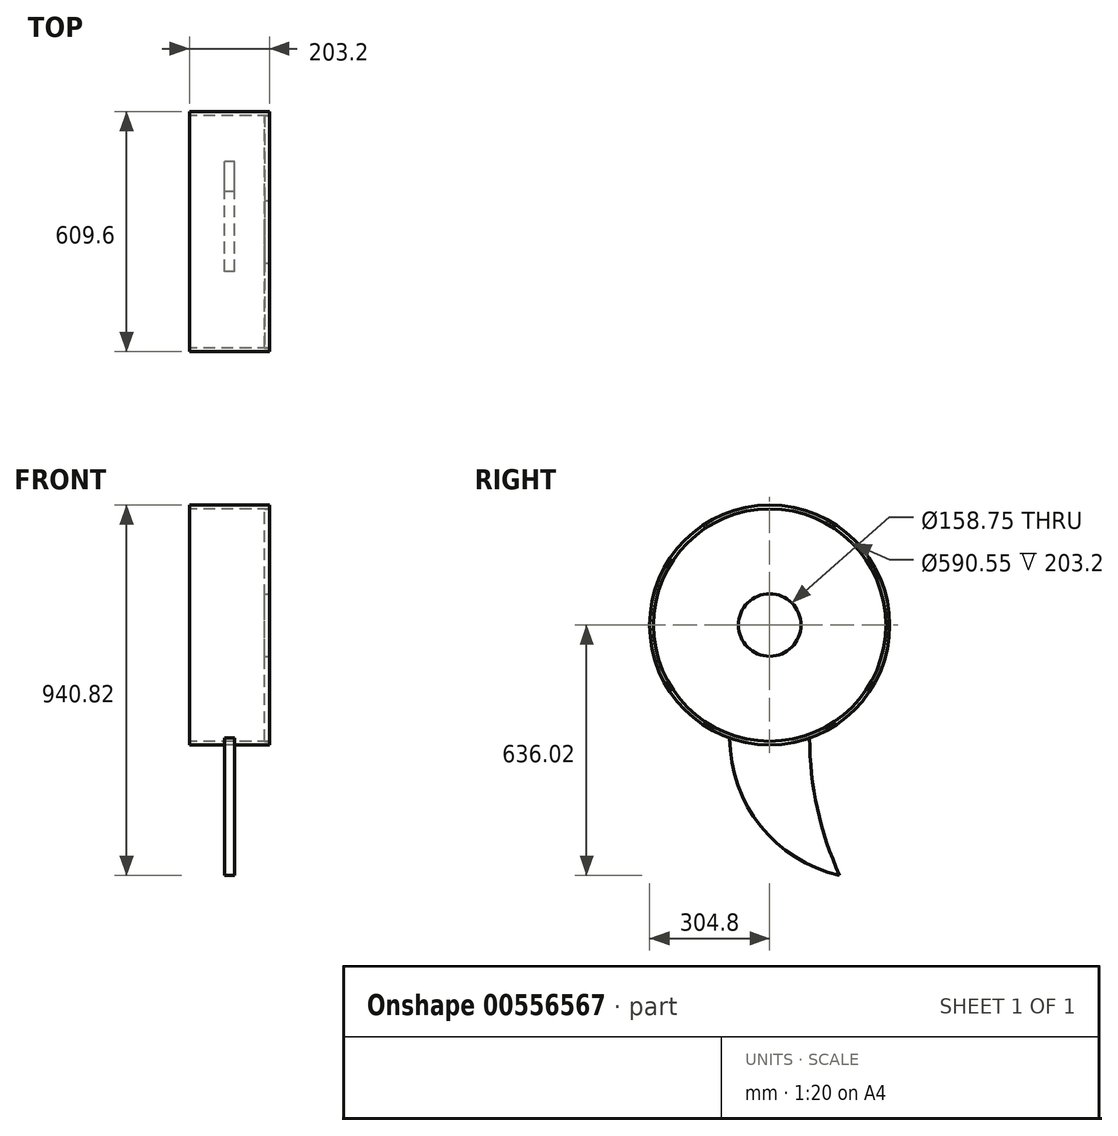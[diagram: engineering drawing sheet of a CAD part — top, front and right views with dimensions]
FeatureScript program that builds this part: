
annotation { "Feature Type Name" : "Feature", "Feature Type Description" : "" }
export const myFeature = defineFeature(function(context is Context, id is Id, definition is map)
    precondition{}
    {
        {
            var Q0;
            Q0=qCreatedBy(makeId("Right.planeOp"),FACE);
            var sketch = newSketch(context, id + "F0", { "sketchPlane" : qUnion([Q0])});
            skCircle(sketch, "E0", {"center": v(0, 0) * mm, "radius": 101.6 * mm, "construction": true});
            skCircle(sketch, "E1.0", {"center": v(0, 0) * mm, "radius": 660.4 * mm, "construction": true});
            skCircle(sketch, "E2", {"center": v(0, 0) * mm, "radius": 76.2 * mm, "construction": true});
            skCircle(sketch, "E3.0", {"center": v(0, 0) * mm, "radius": 304.8 * mm, "construction": true});
            skLineSegment(sketch, "E4.bottom", {"start": v(-101.6, -287.37) * mm, "end": v(101.6, -287.37) * mm, "construction": true});
            skLineSegment(sketch, "E4.top", {"start": v(-101.6, -660.4) * mm, "end": v(101.6, -660.4) * mm, "construction": true});
            skLineSegment(sketch, "E4.left", {"start": v(-101.6, -287.37) * mm, "end": v(-101.6, -660.4) * mm, "construction": true});
            skLineSegment(sketch, "E4.right", {"start": v(101.6, -287.37) * mm, "end": v(101.6, -660.4) * mm, "construction": true});
            skLineSegment(sketch, "E5", {"start": v(177.8, 247.57) * mm, "end": v(177.8, -636.02) * mm, "construction": true});
            skArc(sketch, "E6", {"start": v(-101.6, -287.37) * mm, "mid": v(-23.13, -510.76) * mm, "end": v(177.8, -636.02) * mm});
            skArc(sketch, "E7", {"start": v(101.6, -287.37) * mm, "mid": v(120.87, -465.8) * mm, "end": v(177.8, -636.02) * mm});
            skArc(sketch, "E8", {"start": v(-101.6, -287.37) * mm, "mid": v(0, -304.8) * mm, "end": v(101.6, -287.37) * mm});
            skSolve(sketch);
        }
        {
            var Q0;
            Q0 = qSketchRegion(id + "F0", true);
            extrude(context, id + "F1", {"entities" : qUnion([Q0]), "endBound" : BoundingType.SYMMETRIC, "depth" : 25.4 * mm, "offsetDistance" : 25.4 * mm});
        }
        {
            var Q0;
            Q0=qCreatedBy(makeId("Right.planeOp"),FACE);
            var sketch = newSketch(context, id + "F2", { "sketchPlane" : qUnion([Q0])});
            skCircle(sketch, "E9", {"center": v(0, 0) * mm, "radius": 304.8 * mm});
            skCircle(sketch, "E10.0", {"center": v(0, 0) * mm, "radius": 295.28 * mm});
            skSolve(sketch);
        }
        {
            var Q0;
            Q0 = qSketchRegion(id + "F2", true);
            extrude(context, id + "F3", {"entities" : qUnion([Q0]), "endBound" : BoundingType.SYMMETRIC, "depth" : 203.2 * mm, "offsetDistance" : 25.4 * mm});
        }
        {
            var Q0;
            Q0=makeQuery(id+"F3.opExtrude","CAP_FACE",FACE,{"disambiguationData":[OSD([sQuery(id+"F2.wireOp",EDGE,"E9"),sQuery(id+"F2.wireOp",EDGE,"E10.0")])],"isStart":false});
            var sketch = newSketch(context, id + "F4", { "sketchPlane" : qUnion([Q0])});
            skCircle(sketch, "E11", {"center": v(0, 0) * mm, "radius": 295.28 * mm});
            skCircle(sketch, "E12", {"center": v(0, 0) * mm, "radius": 79.38 * mm});
            skSolve(sketch);
        }
        {
            var Q0;
            Q0 = qSketchRegion(id + "F4", true);
            extrude(context, id + "F5", {"entities" : qUnion([Q0]), "oppositeDirection" : true, "depth" : 12.7 * mm, "offsetDistance" : 25.4 * mm});
        }
    });
